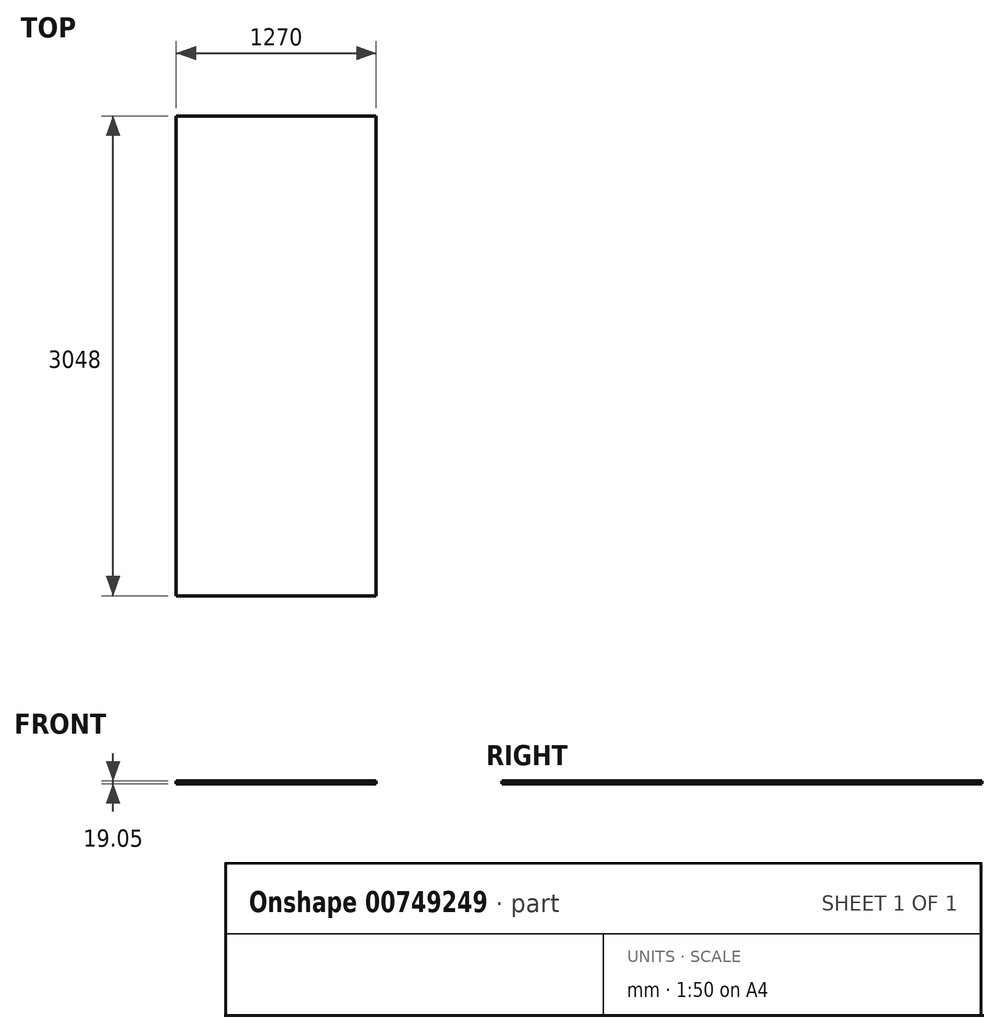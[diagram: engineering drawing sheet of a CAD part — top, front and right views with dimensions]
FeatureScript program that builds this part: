
annotation { "Feature Type Name" : "Feature", "Feature Type Description" : "" }
export const myFeature = defineFeature(function(context is Context, id is Id, definition is map)
    precondition{}
    {
        {
            var Q0;
            Q0=qCreatedBy(makeId("Top.planeOp"),FACE);
            var sketch = newSketch(context, id + "F0", { "sketchPlane" : qUnion([Q0])});
            skLineSegment(sketch, "E0.bottom", {"start": v(635, 1524) * mm, "end": v(-635, 1524) * mm});
            skLineSegment(sketch, "E0.top", {"start": v(635, -1524) * mm, "end": v(-635, -1524) * mm});
            skLineSegment(sketch, "E0.left", {"start": v(635, 1524) * mm, "end": v(635, -1524) * mm});
            skLineSegment(sketch, "E0.right", {"start": v(-635, 1524) * mm, "end": v(-635, -1524) * mm});
            skPoint(sketch, "E0.middle", {"position": v(0, 0) * mm});
            skSolve(sketch);
        }
        {
            var Q0;
            Q0 = qSketchRegion(id + "F0", true);
            extrude(context, id + "F1", {"entities" : qUnion([Q0]), "depth" : 19.05 * mm, "offsetDistance" : 25.4 * mm});
        }
    });
